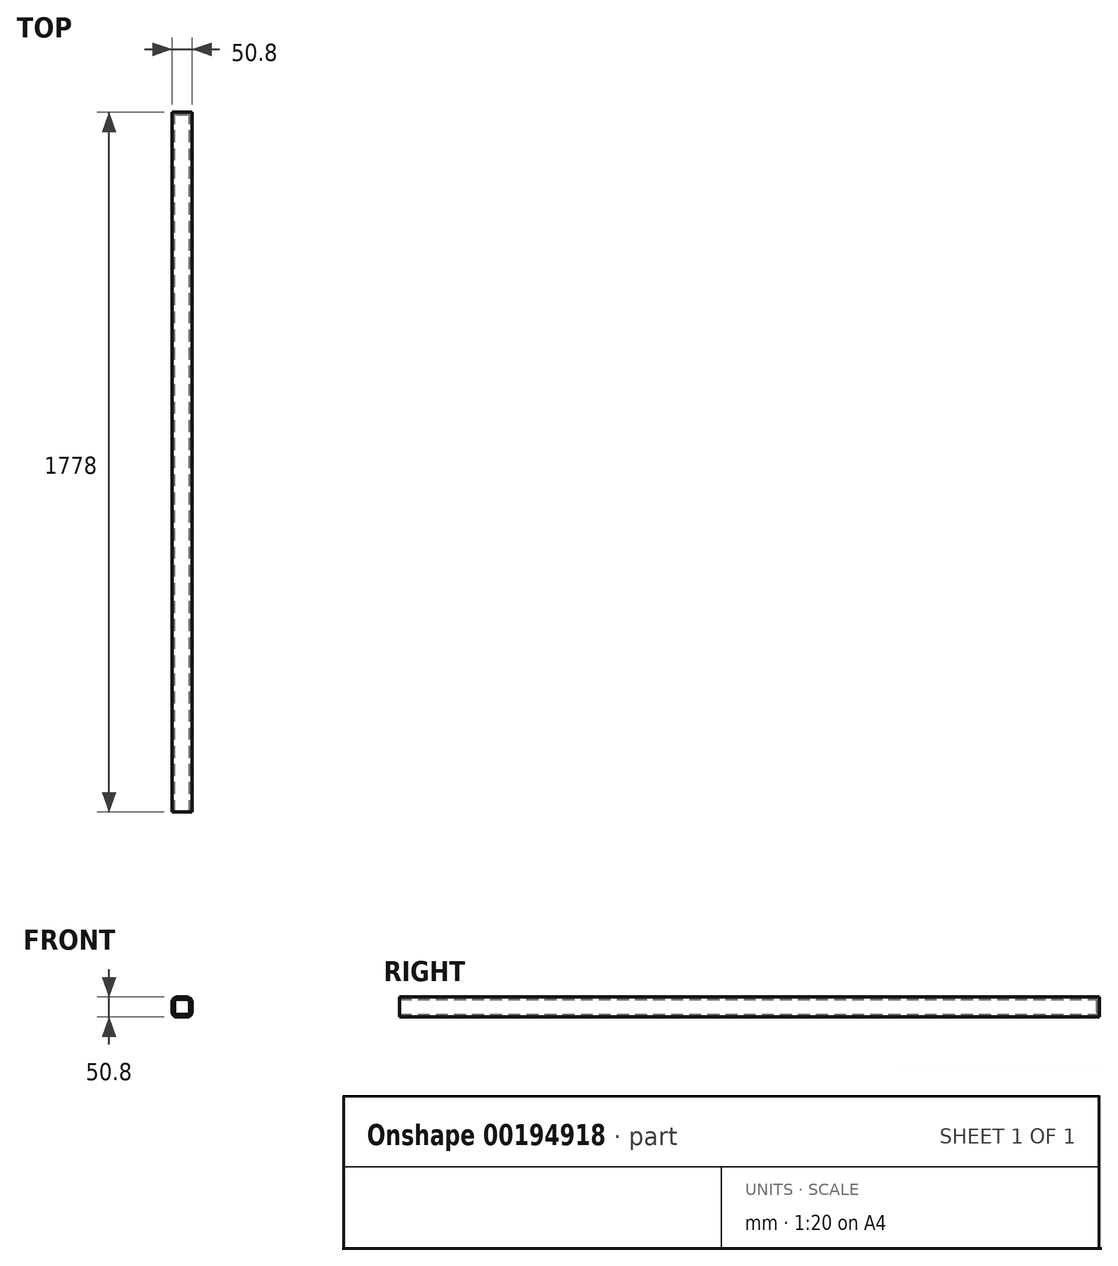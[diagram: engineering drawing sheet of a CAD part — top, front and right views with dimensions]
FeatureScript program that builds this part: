
annotation { "Feature Type Name" : "Feature", "Feature Type Description" : "" }
export const myFeature = defineFeature(function(context is Context, id is Id, definition is map)
    precondition{}
    {
        {
            var Q0;
            Q0=qCreatedBy(makeId("Front.planeOp"),FACE);
            var sketch = newSketch(context, id + "F0", { "sketchPlane" : qUnion([Q0])});
            skLineSegment(sketch, "E0.bottom", {"start": v(0, 0) * mm, "end": v(50.8, 0) * mm});
            skLineSegment(sketch, "E0.top", {"start": v(0, 50.8) * mm, "end": v(50.8, 50.8) * mm});
            skLineSegment(sketch, "E0.left", {"start": v(0, 0) * mm, "end": v(0, 50.8) * mm});
            skLineSegment(sketch, "E0.right", {"start": v(50.8, 0) * mm, "end": v(50.8, 50.8) * mm});
            skSolve(sketch);
        }
        {
            var Q0;
            Q0=makeQuery(id+"F0.imprint","IMPRINT",FACE,{"disambiguationData":[TD([[makeQuery(id+"F0.imprint","IMPRINT",EDGE,{"derivedFrom":sQuery(id+"F0.wireOp",EDGE,"E0.bottom")}),1.0]])]});
            var sketch = newSketch(context, id + "F1", { "sketchPlane" : qUnion([Q0])});
            skSolve(sketch);
        }
        {
            var Q0;
            Q0=makeQuery(id+"F1.imprint","IMPRINT",FACE,{"disambiguationData":[TD([[makeQuery(id+"F1.imprint","IMPRINT",EDGE,{"derivedFrom":makeQuery(id+"F0.imprint","IMPRINT",EDGE,{"derivedFrom":sQuery(id+"F0.wireOp",EDGE,"E0.bottom")})}),1.0]])]});
            extrude(context, id + "F2", {"entities" : qUnion([Q0]), "depth" : 1778 * mm, "offsetDistance" : 25.4 * mm});
        }
        {
            var Q0;
            Q0=makeQuery(id+"F2.opExtrude","SWEPT_EDGE",EDGE,{"disambiguationData":[OSD([sQuery(id+"F0.wireOp",EDGE,"E0.top"),sQuery(id+"F0.wireOp",EDGE,"E0.left")])]});
            var Q1;
            Q1=makeQuery(id+"F2.opExtrude","SWEPT_EDGE",EDGE,{"disambiguationData":[OSD([sQuery(id+"F0.wireOp",EDGE,"E0.bottom"),sQuery(id+"F0.wireOp",EDGE,"E0.left")])]});
            var Q2;
            Q2=makeQuery(id+"F2.opExtrude","SWEPT_EDGE",EDGE,{"disambiguationData":[OSD([sQuery(id+"F0.wireOp",EDGE,"E0.top"),sQuery(id+"F0.wireOp",EDGE,"E0.right")])]});
            var Q3;
            Q3=makeQuery(id+"F2.opExtrude","SWEPT_EDGE",EDGE,{"disambiguationData":[OSD([sQuery(id+"F0.wireOp",EDGE,"E0.bottom"),sQuery(id+"F0.wireOp",EDGE,"E0.right")])]});
            fillet(context, id + "F3", {"entities" : qUnion([Q0, Q1, Q2, Q3]), "radius" : 12.7 * mm, "tangentPropagation" : true, "allowEdgeOverflow" : false});
        }
        {
            var Q0;
            Q0=makeQuery(id+"F2.opExtrude","CAP_FACE",FACE,{"disambiguationData":[OSD([sQuery(id+"F0.wireOp",EDGE,"E0.bottom"),sQuery(id+"F0.wireOp",EDGE,"E0.top"),sQuery(id+"F0.wireOp",EDGE,"E0.left"),sQuery(id+"F0.wireOp",EDGE,"E0.right")])],"isStart":false});
            shell(context, id + "F4", {"entities" : qUnion([Q0]), "thickness" : 6.35 * mm});
        }
    });
